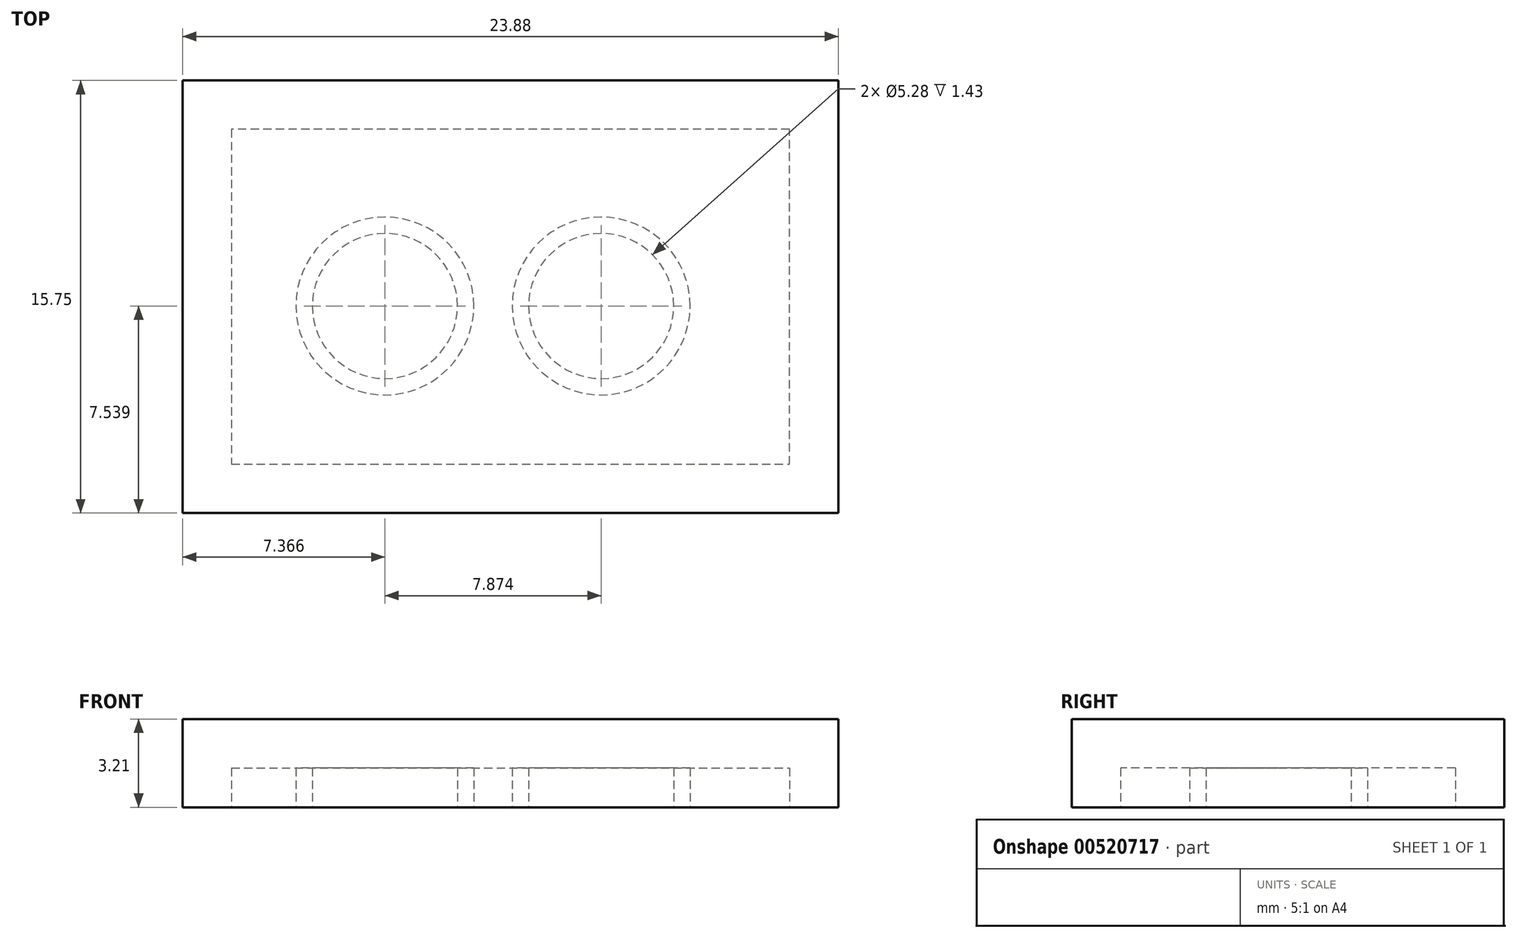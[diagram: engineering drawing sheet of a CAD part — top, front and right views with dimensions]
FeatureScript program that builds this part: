
annotation { "Feature Type Name" : "Feature", "Feature Type Description" : "" }
export const myFeature = defineFeature(function(context is Context, id is Id, definition is map)
    precondition{}
    {
        {
            var Q0;
            Q0=qCreatedBy(makeId("Top.planeOp"),FACE);
            var sketch = newSketch(context, id + "F0", { "sketchPlane" : qUnion([Q0])});
            skLineSegment(sketch, "E0", {"start": v(0, 0) * mm, "end": v(23.88, 0) * mm});
            skLineSegment(sketch, "E1", {"start": v(23.88, 0) * mm, "end": v(23.88, 15.75) * mm});
            skLineSegment(sketch, "E2", {"start": v(23.88, 15.75) * mm, "end": v(0, 15.75) * mm});
            skLineSegment(sketch, "E3", {"start": v(0, 15.75) * mm, "end": v(0, 0) * mm});
            skSolve(sketch);
        }
        {
            var Q0;
            Q0=qSketchRegion(id+"F2",true);
            var Q1;
            Q1=makeQuery(id+"F0.imprint","IMPRINT",FACE,{"disambiguationData":[TD([[makeQuery(id+"F0.imprint","IMPRINT",EDGE,{"derivedFrom":sQuery(id+"F0.wireOp",EDGE,"E0")}),1.0]])]});
            extrude(context, id + "F1", {"entities" : qUnion([Q0, Q1]), "depth" : 3.2 * mm});
        }
        {
            var Q0;
            Q0=makeQuery(id+"F1.opExtrude","CAP_FACE",FACE,{"disambiguationData":[OSD([sQuery(id+"F0.wireOp",EDGE,"E0"),sQuery(id+"F0.wireOp",EDGE,"E1"),sQuery(id+"F0.wireOp",EDGE,"E2"),sQuery(id+"F0.wireOp",EDGE,"E3")])],"isStart":false});
            var sketch = newSketch(context, id + "F2", { "sketchPlane" : qUnion([Q0])});
            skCircle(sketch, "E4", {"center": v(3.4, 11.86) * mm, "radius": 2.41 * mm});
            skCircle(sketch, "E5", {"center": v(11.27, 11.86) * mm, "radius": 2.42 * mm});
            skCircle(sketch, "E6", {"center": v(19.15, 11.86) * mm, "radius": 2.42 * mm});
            skCircle(sketch, "E7", {"center": v(3.4, 3.94) * mm, "radius": 2.41 * mm});
            skCircle(sketch, "E8", {"center": v(11.27, 3.94) * mm, "radius": 2.41 * mm});
            skCircle(sketch, "E9", {"center": v(19.15, 3.94) * mm, "radius": 2.41 * mm});
            skSolve(sketch);
        }
        {
            var Q0;
            Q0=makeQuery(id+"F1.opExtrude","CAP_FACE",FACE,{"disambiguationData":[OSD([sQuery(id+"F0.wireOp",EDGE,"E0"),sQuery(id+"F0.wireOp",EDGE,"E1"),sQuery(id+"F0.wireOp",EDGE,"E2"),sQuery(id+"F0.wireOp",EDGE,"E3")])],"isStart":true});
            shell(context, id + "F3", {"entities" : qUnion([Q0]), "thickness" : 1.78 * mm});
        }
        {
            var Q0;
            Q0=makeQuery(id+"F0.imprint","IMPRINT",FACE,{"disambiguationData":[TD([[makeQuery(id+"F0.imprint","IMPRINT",EDGE,{"derivedFrom":sQuery(id+"F0.wireOp",EDGE,"E0")}),1.0]])]});
            var sketch = newSketch(context, id + "F4", { "sketchPlane" : qUnion([Q0])});
            skCircle(sketch, "E10", {"center": v(7.37, 7.54) * mm, "radius": 3.24 * mm});
            skCircle(sketch, "E11", {"center": v(15.24, 7.54) * mm, "radius": 3.24 * mm});
            skCircle(sketch, "E12", {"center": v(7.37, 7.54) * mm, "radius": 2.64 * mm});
            skCircle(sketch, "E13", {"center": v(15.24, 7.54) * mm, "radius": 2.64 * mm});
            skLineSegment(sketch, "E14", {"start": v(7.37, 7.54) * mm, "end": v(0, 7.54) * mm});
            skSolve(sketch);
        }
        {
            var Q0;
            Q0=qSketchRegion(id+"F4",true);
            extrude(context, id + "F5", {"entities" : qUnion([Q0]), "operationType" : NewBodyOperationType.ADD, "depth" : 3.07 * mm});
        }
    });
